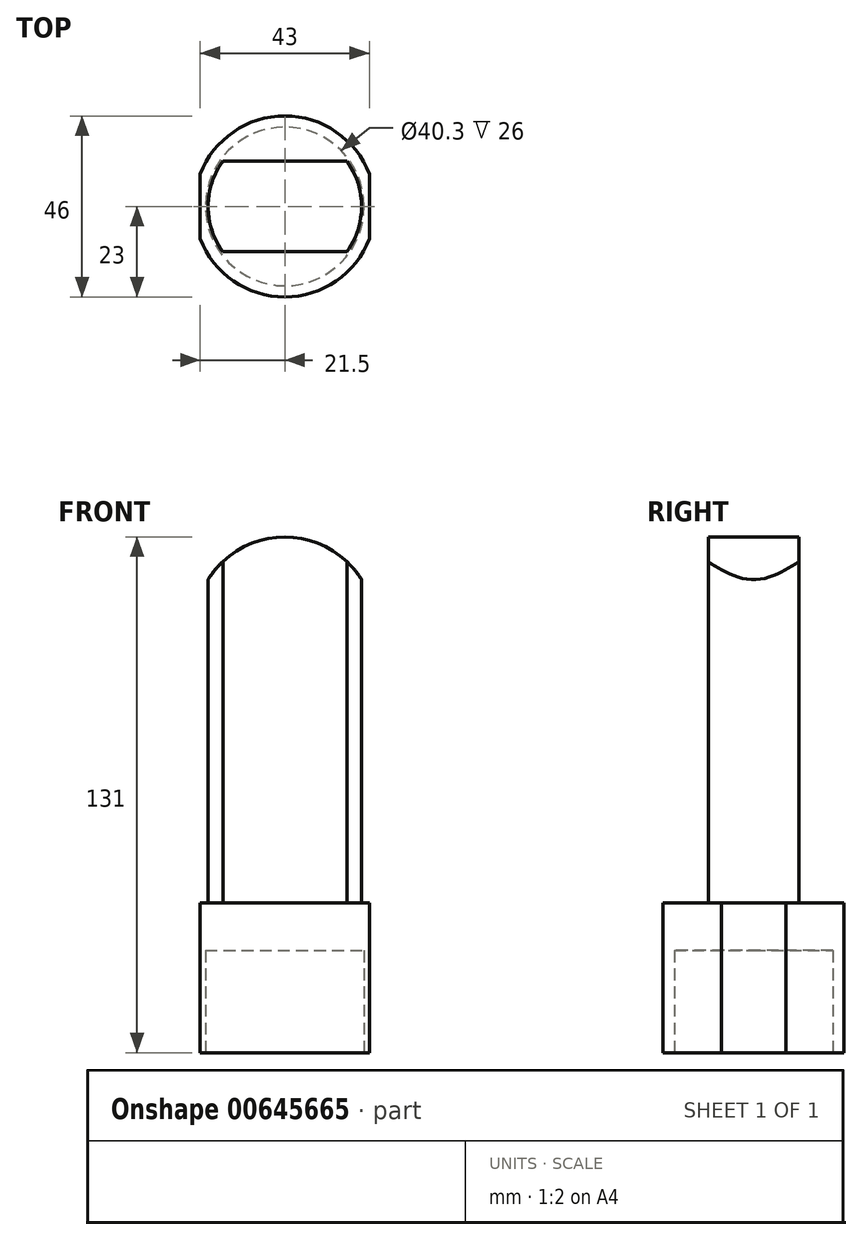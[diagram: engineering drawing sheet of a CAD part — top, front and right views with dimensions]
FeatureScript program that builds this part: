
annotation { "Feature Type Name" : "Feature", "Feature Type Description" : "" }
export const myFeature = defineFeature(function(context is Context, id is Id, definition is map)
    precondition{}
    {
        {
            var Q0;
            Q0=qCreatedBy(makeId("Top.planeOp"),FACE);
            var sketch = newSketch(context, id + "F0", { "sketchPlane" : qUnion([Q0])});
            skArc(sketch, "E0", {"start": v(21.5, 8.17) * mm, "mid": v(0, 23) * mm, "end": v(-21.5, 8.17) * mm});
            skPoint(sketch, "E1", {"position": v(21.5, 8.17) * mm});
            skLineSegment(sketch, "E2", {"start": v(21.5, 8.17) * mm, "end": v(21.5, -8.17) * mm});
            skLineSegment(sketch, "E3.MirrorCS", {"start": v(-21.5, 8.17) * mm, "end": v(-21.5, -8.17) * mm});
            skArc(sketch, "E4.trimOffspring", {"start": v(-21.5, -8.17) * mm, "mid": v(0, -23) * mm, "end": v(21.5, -8.17) * mm});
            skSolve(sketch);
        }
        {
            var Q0;
            Q0=makeQuery(id+"F0.imprint","IMPRINT",FACE,{"disambiguationData":[TD([[makeQuery(id+"F0.imprint","IMPRINT",EDGE,{"derivedFrom":sQuery(id+"F0.wireOp",EDGE,"E0")}),1.0]])]});
            extrude(context, id + "F1", {"entities" : qUnion([Q0]), "depth" : 38 * mm, "offsetDistance" : 25 * mm});
        }
        {
            var Q0;
            Q0=makeQuery(id+"F1.opExtrude","CAP_FACE",FACE,{"disambiguationData":[OSD([sQuery(id+"F0.wireOp",EDGE,"E0"),sQuery(id+"F0.wireOp",EDGE,"E2"),sQuery(id+"F0.wireOp",EDGE,"E3.MirrorCS"),sQuery(id+"F0.wireOp",EDGE,"E4.trimOffspring")])],"isStart":true});
            var sketch = newSketch(context, id + "F2", { "sketchPlane" : qUnion([Q0])});
            skCircle(sketch, "E5", {"center": v(0, 0) * mm, "radius": 20.15 * mm});
            skSolve(sketch);
        }
        {
            var Q0;
            Q0=makeQuery(id+"F2.imprint","IMPRINT",FACE,{"disambiguationData":[TD([[makeQuery(id+"F2.imprint","IMPRINT",EDGE,{"derivedFrom":sQuery(id+"F2.wireOp",EDGE,"E5")}),1.0]])]});
            extrude(context, id + "F3", {"entities" : qUnion([Q0]), "operationType" : NewBodyOperationType.REMOVE, "oppositeDirection" : true, "depth" : 26 * mm, "offsetDistance" : 25 * mm});
        }
        {
            var Q0;
            Q0=makeQuery(id+"F1.opExtrude","CAP_FACE",FACE,{"disambiguationData":[OSD([sQuery(id+"F0.wireOp",EDGE,"E0"),sQuery(id+"F0.wireOp",EDGE,"E2"),sQuery(id+"F0.wireOp",EDGE,"E3.MirrorCS"),sQuery(id+"F0.wireOp",EDGE,"E4.trimOffspring")])],"isStart":false});
            var sketch = newSketch(context, id + "F4", { "sketchPlane" : qUnion([Q0])});
            skArc(sketch, "E6", {"start": v(15.75, -11.5) * mm, "mid": v(19.5, 0) * mm, "end": v(15.75, 11.5) * mm});
            skLineSegment(sketch, "E7", {"start": v(0, -11.5) * mm, "end": v(-15.75, -11.5) * mm});
            skLineSegment(sketch, "E8.MirrorCS", {"start": v(0, -11.5) * mm, "end": v(15.75, -11.5) * mm});
            skLineSegment(sketch, "E9.MirrorCS", {"start": v(0, 11.5) * mm, "end": v(-15.75, 11.5) * mm});
            skLineSegment(sketch, "E10.MirrorCS", {"start": v(0, 11.5) * mm, "end": v(15.75, 11.5) * mm});
            skArc(sketch, "E11.trimOffspring", {"start": v(-15.75, 11.5) * mm, "mid": v(-19.5, 0) * mm, "end": v(-15.75, -11.5) * mm});
            skSolve(sketch);
        }
        {
            var Q0;
            Q0=makeQuery(id+"F4.imprint","IMPRINT",FACE,{"disambiguationData":[TD([[makeQuery(id+"F4.imprint","IMPRINT",EDGE,{"derivedFrom":sQuery(id+"F4.wireOp",EDGE,"E6")}),1.0]])]});
            extrude(context, id + "F5", {"entities" : qUnion([Q0]), "operationType" : NewBodyOperationType.ADD, "depth" : 93 * mm, "offsetDistance" : 25 * mm});
        }
        {
            var Q0;
            Q0=makeQuery(id+"F5.opExtrude","SWEPT_FACE",FACE,{"disambiguationData":[OSD([sQuery(id+"F4.wireOp",EDGE,"E9.MirrorCS"),sQuery(id+"F4.wireOp",EDGE,"E10.MirrorCS")])]});
            var sketch = newSketch(context, id + "F6", { "sketchPlane" : qUnion([Q0])});
            skPoint(sketch, "E12", {"position": v(0, 108) * mm});
            skArc(sketch, "E13", {"start": v(22.92, 109.94) * mm, "mid": v(1.2, 130.97) * mm, "end": v(-22.6, 112.3) * mm});
            skLineSegment(sketch, "E14", {"start": v(-22.6, 112.3) * mm, "end": v(-46.5, 143.33) * mm});
            skLineSegment(sketch, "E15", {"start": v(-46.5, 143.33) * mm, "end": v(59.5, 143.33) * mm});
            skLineSegment(sketch, "E16", {"start": v(59.5, 143.33) * mm, "end": v(22.92, 109.94) * mm});
            skSolve(sketch);
        }
        {
            var Q0;
            {var subQ0=sQuery(id+"F6.wireOp",EDGE,"E14");Q0=makeQuery(id+"F6.imprint","IMPRINT",FACE,{"disambiguationData":[TD([[makeQuery(id+"F6.imprint","IMPRINT",EDGE,{"derivedFrom":subQ0}),-1.0]])]});}
            var Q1;
            {var subQ0=sQuery(id+"F6.wireOp",EDGE,"E13");var subQ1=sQuery(id+"F4.wireOp",EDGE,"E9.MirrorCS");var subQ2=makeQuery(id+"F5.opExtrude","SWEPT_EDGE",EDGE,{"disambiguationData":[OSD([subQ1,sQuery(id+"F4.wireOp",EDGE,"E11.trimOffspring")])]});var subQ3=makeQuery(id+"F6.imprint","INTERSECT",VERTEX,{"derivedFrom":[subQ2,subQ0]});Q1=makeQuery(id+"F6.imprint","IMPRINT",FACE,{"disambiguationData":[TD([[makeQuery(id+"F6.imprint","IMPRINT",EDGE,{"disambiguationData":[TD([[subQ3,-1.0]])],"derivedFrom":subQ0}),-1.0]])]});}
            var Q2;
            {var subQ0=sQuery(id+"F6.wireOp",EDGE,"E13");var subQ1=sQuery(id+"F4.wireOp",EDGE,"E10.MirrorCS");var subQ2=makeQuery(id+"F5.opExtrude","SWEPT_EDGE",EDGE,{"disambiguationData":[OSD([sQuery(id+"F4.wireOp",EDGE,"E6"),subQ1])]});var subQ3=makeQuery(id+"F6.imprint","INTERSECT",VERTEX,{"derivedFrom":[subQ2,subQ0]});Q2=makeQuery(id+"F6.imprint","IMPRINT",FACE,{"disambiguationData":[TD([[makeQuery(id+"F6.imprint","IMPRINT",EDGE,{"disambiguationData":[TD([[subQ3,1.0]])],"derivedFrom":subQ0}),-1.0]])]});}
            extrude(context, id + "F7", {"entities" : qUnion([Q0, Q1, Q2]), "operationType" : NewBodyOperationType.REMOVE, "endBound" : BoundingType.THROUGH_ALL, "oppositeDirection" : true, "depth" : 25 * mm, "offsetDistance" : 25 * mm});
        }
    });
